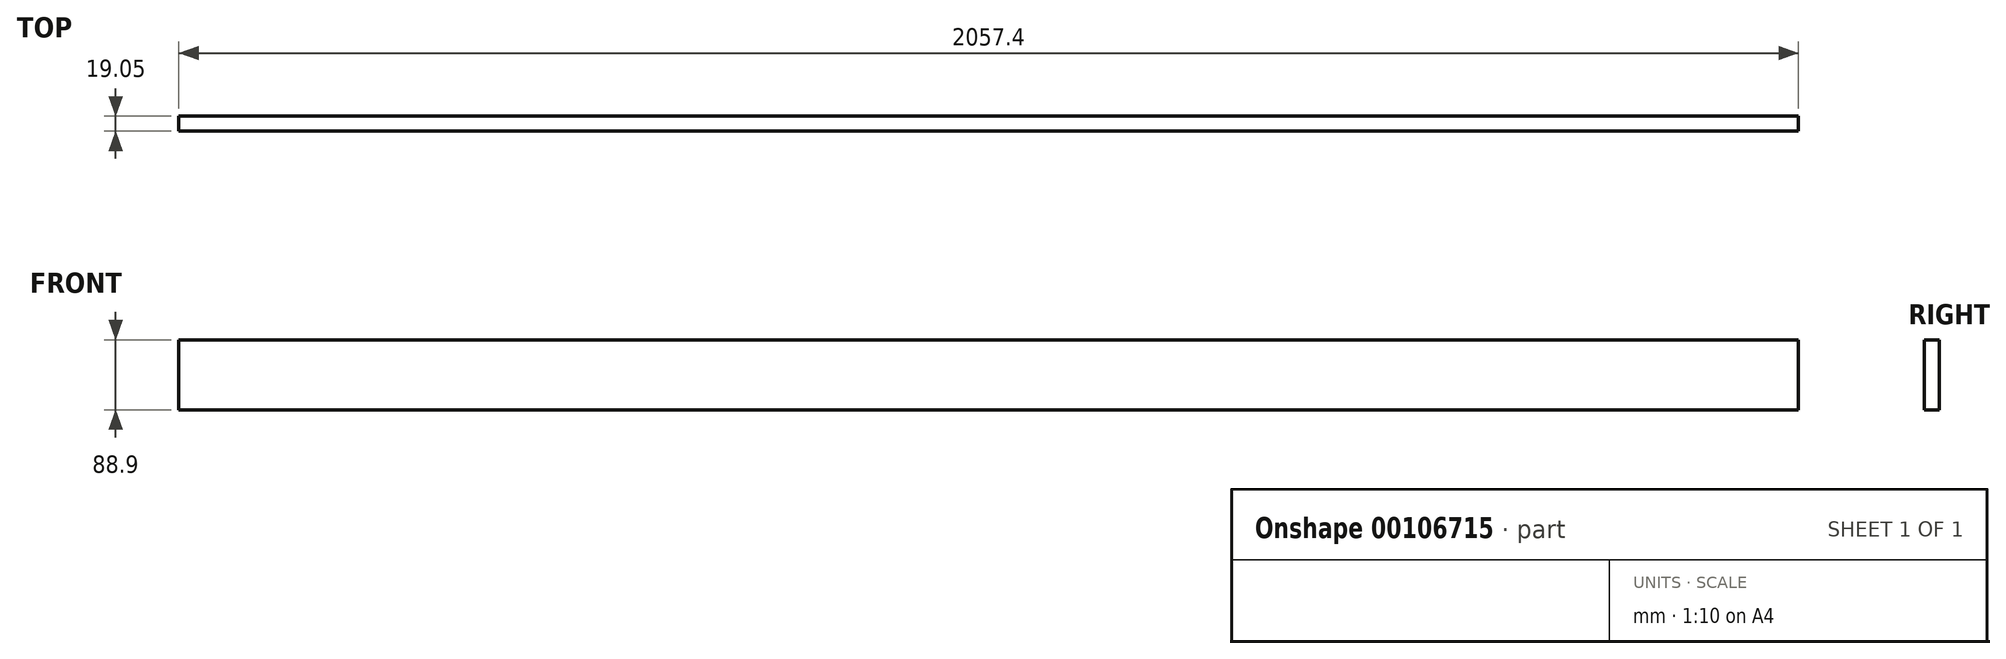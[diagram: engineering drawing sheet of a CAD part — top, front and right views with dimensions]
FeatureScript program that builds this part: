
annotation { "Feature Type Name" : "Feature", "Feature Type Description" : "" }
export const myFeature = defineFeature(function(context is Context, id is Id, definition is map)
    precondition{}
    {
        {
            var Q0;
            Q0=qCreatedBy(makeId("Front.planeOp"),FACE);
            var sketch = newSketch(context, id + "F0", { "sketchPlane" : qUnion([Q0])});
            skLineSegment(sketch, "E0.bottom", {"start": v(0, 0) * mm, "end": v(2057.4, 0) * mm});
            skLineSegment(sketch, "E0.top", {"start": v(0, 88.9) * mm, "end": v(2057.4, 88.9) * mm});
            skLineSegment(sketch, "E0.left", {"start": v(0, 0) * mm, "end": v(0, 88.9) * mm});
            skLineSegment(sketch, "E0.right", {"start": v(2057.4, 0) * mm, "end": v(2057.4, 88.9) * mm});
            skSolve(sketch);
        }
        {
            var Q0;
            Q0=makeQuery(id+"F0.imprint","IMPRINT",FACE,{"disambiguationData":[TD([[makeQuery(id+"F0.imprint","IMPRINT",EDGE,{"derivedFrom":sQuery(id+"F0.wireOp",EDGE,"E0.bottom")}),1.0]])]});
            extrude(context, id + "F1", {"entities" : qUnion([Q0]), "depth" : 19.05 * mm});
        }
    });
